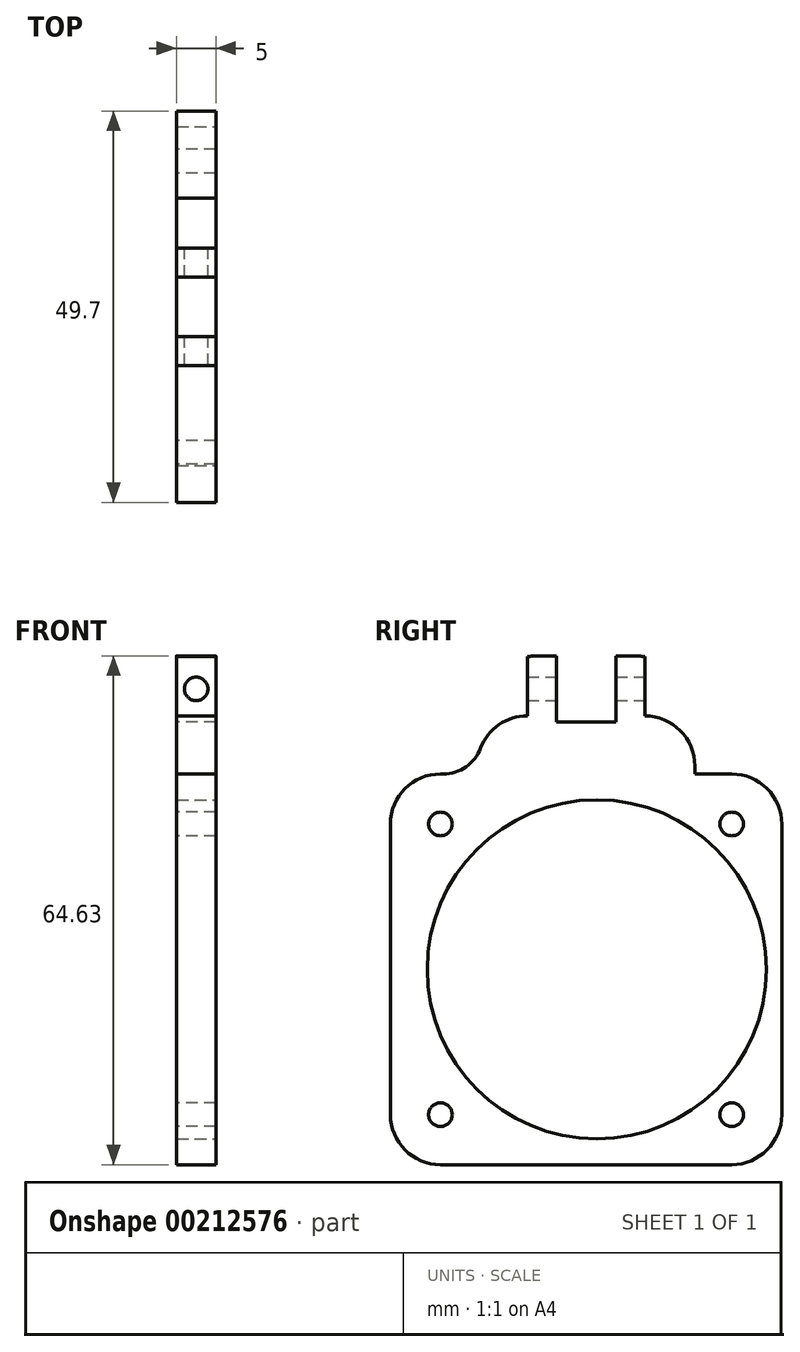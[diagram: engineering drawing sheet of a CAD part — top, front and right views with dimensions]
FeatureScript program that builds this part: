
annotation { "Feature Type Name" : "Feature", "Feature Type Description" : "" }
export const myFeature = defineFeature(function(context is Context, id is Id, definition is map)
    precondition{}
    {
        {
            var Q0;
            Q0=qCreatedBy(makeId("Right.planeOp"),FACE);
            var sketch = newSketch(context, id + "F0", { "sketchPlane" : qUnion([Q0])});
            skCircle(sketch, "E0", {"center": v(0, 0) * mm, "radius": 1.5 * mm});
            skCircle(sketch, "E1", {"center": v(0, -36.93) * mm, "radius": 1.5 * mm});
            skCircle(sketch, "E2", {"center": v(37, -36.93) * mm, "radius": 1.5 * mm});
            skCircle(sketch, "E3", {"center": v(37, 0) * mm, "radius": 1.5 * mm});
            skLineSegment(sketch, "E4", {"start": v(0, 0) * mm, "end": v(0, -36.93) * mm});
            skLineSegment(sketch, "E5.0", {"start": v(-6.35, 0) * mm, "end": v(-6.35, -36.93) * mm});
            skLineSegment(sketch, "E6", {"start": v(0, 0) * mm, "end": v(37, 0) * mm});
            skLineSegment(sketch, "E7", {"start": v(37, -36.93) * mm, "end": v(0, -36.93) * mm});
            skLineSegment(sketch, "E8", {"start": v(37, -36.93) * mm, "end": v(37, -1.5) * mm});
            skLineSegment(sketch, "E9.0", {"start": v(0, 6.35) * mm, "end": v(37, 6.35) * mm});
            skLineSegment(sketch, "E10.0", {"start": v(43.35, -36.93) * mm, "end": v(43.35, 0) * mm});
            skLineSegment(sketch, "E11.0", {"start": v(37, -43.28) * mm, "end": v(0, -43.28) * mm});
            skArc(sketch, "E12.filletArc", {"start": v(-6.35, -36.93) * mm, "mid": v(-4.5, -41.42) * mm, "end": v(0, -43.28) * mm});
            skArc(sketch, "E13.filletArc", {"start": v(37, -43.28) * mm, "mid": v(41.5, -41.42) * mm, "end": v(43.35, -36.93) * mm});
            skArc(sketch, "E14.filletArc", {"start": v(0, 6.35) * mm, "mid": v(-4.5, 4.5) * mm, "end": v(-6.35, 0) * mm});
            skArc(sketch, "E15.filletArc", {"start": v(43.35, 0) * mm, "mid": v(41.5, 4.5) * mm, "end": v(37, 6.35) * mm});
            skSolve(sketch);
        }
        {
            var Q0;
            Q0=qSketchRegion(id+"F0",true);
            var Q1;
            {var subQ5=sQuery(id+"F0.wireOp",EDGE,"E0");var subQ11=sQuery(id+"F0.wireOp",EDGE,"E4");var subQ15=makeQuery(id+"F0.imprint","INTERSECT",VERTEX,{"derivedFrom":[subQ5,subQ11]});Q1=makeQuery(id+"F0.imprint","IMPRINT",FACE,{"disambiguationData":[TD([[makeQuery(id+"F0.imprint","IMPRINT",EDGE,{"disambiguationData":[TD([[subQ15,-1.0]])],"derivedFrom":subQ5}),-1.0]])]});}
            extrude(context, id + "F1", {"entities" : qUnion([Q0, Q1]), "depth" : 5 * mm});
        }
        {
            var Q0;
            Q0=makeQuery(id+"F1.opExtrude","CAP_FACE",FACE,{"disambiguationData":[OSD([sQuery(id+"F0.wireOp",EDGE,"E0"),sQuery(id+"F0.wireOp",EDGE,"E1"),sQuery(id+"F0.wireOp",EDGE,"E2"),sQuery(id+"F0.wireOp",EDGE,"E3"),sQuery(id+"F0.wireOp",EDGE,"E5.0"),sQuery(id+"F0.wireOp",EDGE,"E9.0"),sQuery(id+"F0.wireOp",EDGE,"E10.0"),sQuery(id+"F0.wireOp",EDGE,"E11.0"),sQuery(id+"F0.wireOp",EDGE,"E12.filletArc"),sQuery(id+"F0.wireOp",EDGE,"E13.filletArc"),sQuery(id+"F0.wireOp",EDGE,"E14.filletArc"),sQuery(id+"F0.wireOp",EDGE,"E15.filletArc")])],"isStart":false});
            var sketch = newSketch(context, id + "F2", { "sketchPlane" : qUnion([Q0])});
            skCircle(sketch, "E16", {"center": v(19.86, -18.46) * mm, "radius": 21.54 * mm});
            skPoint(sketch, "E16.centerSnap0", {"position": v(-6.35, -18.46) * mm});
            skSolve(sketch);
        }
        {
            var Q0;
            Q0=makeQuery(id+"F2.imprint","IMPRINT",FACE,{"disambiguationData":[TD([[makeQuery(id+"F2.imprint","IMPRINT",EDGE,{"derivedFrom":sQuery(id+"F2.wireOp",EDGE,"E16")}),1.0]])]});
            extrude(context, id + "F3", {"entities" : qUnion([Q0]), "operationType" : NewBodyOperationType.REMOVE, "endBound" : BoundingType.THROUGH_ALL, "oppositeDirection" : true, "depth" : 25.4 * mm});
        }
        {
            var Q0;
            Q0=makeQuery(id+"F1.opExtrude","SWEPT_FACE",FACE,{"disambiguationData":[OSD([sQuery(id+"F0.wireOp",EDGE,"E9.0")])]});
            var sketch = newSketch(context, id + "F4", { "sketchPlane" : qUnion([Q0])});
            skLineSegment(sketch, "E17.bottom", {"start": v(5, 32.3) * mm, "end": v(0, 32.3) * mm});
            skLineSegment(sketch, "E17.top", {"start": v(5, 4.7) * mm, "end": v(0, 4.7) * mm});
            skLineSegment(sketch, "E17.left", {"start": v(5, 32.3) * mm, "end": v(5, 4.7) * mm});
            skLineSegment(sketch, "E17.right", {"start": v(0, 32.3) * mm, "end": v(0, 4.7) * mm});
            skPoint(sketch, "E17.middle", {"position": v(2.5, 18.5) * mm});
            skPoint(sketch, "E17.middle.positionSnap0", {"position": v(2.5, 37) * mm});
            skPoint(sketch, "E17.middle.positionSnap1", {"position": v(5, 18.5) * mm});
            skPoint(sketch, "E17.centerSnap0", {"position": v(2.5, 37) * mm});
            skPoint(sketch, "E17.centerSnap1", {"position": v(5, 18.5) * mm});
            skSolve(sketch);
        }
        {
            var Q0;
            Q0=qSketchRegion(id+"F4",true);
            extrude(context, id + "F5", {"entities" : qUnion([Q0]), "operationType" : NewBodyOperationType.ADD, "depth" : 15 * mm});
        }
        {
            var Q0;
            Q0=makeQuery(id+"F5.opExtrude","CAP_EDGE",EDGE,{"disambiguationData":[OSD([sQuery(id+"F4.wireOp",EDGE,"E17.bottom")])],"isStart":false});
            var Q1;
            Q1=makeQuery(id+"F5.opExtrude","CAP_EDGE",EDGE,{"disambiguationData":[OSD([sQuery(id+"F4.wireOp",EDGE,"E17.top")])],"isStart":false});
            fillet(context, id + "F6", {"entities" : qUnion([Q0, Q1]), "radius" : 7.62 * mm, "tangentPropagation" : true, "allowEdgeOverflow" : false});
        }
        {
            var Q0;
            Q0=makeQuery(id+"F5.opExtrude","CAP_FACE",FACE,{"disambiguationData":[OSD([sQuery(id+"F4.wireOp",EDGE,"E17.bottom"),sQuery(id+"F4.wireOp",EDGE,"E17.top"),sQuery(id+"F4.wireOp",EDGE,"E17.left"),sQuery(id+"F4.wireOp",EDGE,"E17.right")])],"isStart":false});
            var sketch = newSketch(context, id + "F7", { "sketchPlane" : qUnion([Q0])});
            skLineSegment(sketch, "E18.bottom", {"start": v(5, 22.27) * mm, "end": v(0, 22.27) * mm});
            skLineSegment(sketch, "E18.top", {"start": v(5, 14.73) * mm, "end": v(0, 14.73) * mm});
            skLineSegment(sketch, "E18.left", {"start": v(5, 22.27) * mm, "end": v(5, 14.73) * mm});
            skLineSegment(sketch, "E18.right", {"start": v(0, 22.27) * mm, "end": v(0, 14.73) * mm});
            skPoint(sketch, "E18.middle", {"position": v(2.5, 18.5) * mm});
            skPoint(sketch, "E18.middle.positionSnap0", {"position": v(2.5, 24.69) * mm});
            skPoint(sketch, "E18.middle.positionSnap1", {"position": v(0, 18.5) * mm});
            skPoint(sketch, "E18.centerSnap0", {"position": v(2.5, 24.69) * mm});
            skPoint(sketch, "E18.centerSnap1", {"position": v(0, 18.5) * mm});
            skSolve(sketch);
        }
        {
            var Q0;
            Q0=qSketchRegion(id+"F7",true);
            extrude(context, id + "F8", {"entities" : qUnion([Q0]), "operationType" : NewBodyOperationType.REMOVE, "oppositeDirection" : true, "depth" : 8.38 * mm});
        }
        {
            var Q0;
            Q0=makeQuery(id+"F8.boolean.opBoolean","COPY",FACE,{"derivedFrom":makeQuery(id+"F8.opExtrude","SWEPT_FACE",FACE,{"disambiguationData":[OSD([sQuery(id+"F7.wireOp",EDGE,"E18.top")])]})});
            var sketch = newSketch(context, id + "F9", { "sketchPlane" : qUnion([Q0])});
            skCircle(sketch, "E19", {"center": v(-2.5, 17.16) * mm, "radius": 1.5 * mm});
            skPoint(sketch, "E19.centerSnap0", {"position": v(0, 17.16) * mm});
            skPoint(sketch, "E19.centerSnap1", {"position": v(-2.5, 21.35) * mm});
            skSolve(sketch);
        }
        {
            var Q0;
            Q0=qSketchRegion(id+"F9",true);
            extrude(context, id + "F10", {"entities" : qUnion([Q0]), "operationType" : NewBodyOperationType.REMOVE, "endBound" : BoundingType.THROUGH_ALL, "oppositeDirection" : true, "depth" : 25.4 * mm, "hasSecondDirection" : true, "secondDirectionBound" : SecondDirectionBoundingType.THROUGH_ALL, "secondDirectionOppositeDirection" : false, "secondDirectionDepth" : 25.4 * mm});
        }
        {
            var Q0;
            Q0=makeQuery(id+"F5.opExtrude","SWEPT_FACE",FACE,{"disambiguationData":[OSD([sQuery(id+"F4.wireOp",EDGE,"E17.bottom")])]});
            var sketch = newSketch(context, id + "F11", { "sketchPlane" : qUnion([Q0])});
            skLineSegment(sketch, "E20.bottom", {"start": v(-5, 13.73) * mm, "end": v(2.36, 13.73) * mm});
            skLineSegment(sketch, "E20.top", {"start": v(-5, 25.82) * mm, "end": v(2.36, 25.82) * mm});
            skLineSegment(sketch, "E20.left", {"start": v(-5, 13.73) * mm, "end": v(-5, 25.82) * mm});
            skLineSegment(sketch, "E20.right", {"start": v(2.36, 13.73) * mm, "end": v(2.36, 25.82) * mm});
            skSolve(sketch);
        }
        {
            var Q0;
            Q0=qSketchRegion(id+"F11",true);
            extrude(context, id + "F12", {"entities" : qUnion([Q0]), "operationType" : NewBodyOperationType.REMOVE, "oppositeDirection" : true, "depth" : 6.35 * mm});
        }
        {
            var Q0;
            Q0=makeQuery(id+"F5.opExtrude","SWEPT_FACE",FACE,{"disambiguationData":[OSD([sQuery(id+"F4.wireOp",EDGE,"E17.top")])]});
            var sketch = newSketch(context, id + "F13", { "sketchPlane" : qUnion([Q0])});
            skLineSegment(sketch, "E21.bottom", {"start": v(5, 13.73) * mm, "end": v(-2.13, 13.73) * mm});
            skLineSegment(sketch, "E21.top", {"start": v(5, 34.68) * mm, "end": v(-2.13, 34.68) * mm});
            skLineSegment(sketch, "E21.left", {"start": v(5, 13.73) * mm, "end": v(5, 34.68) * mm});
            skLineSegment(sketch, "E21.right", {"start": v(-2.13, 13.73) * mm, "end": v(-2.13, 34.68) * mm});
            skSolve(sketch);
        }
        {
            var Q0;
            Q0=qSketchRegion(id+"F13",true);
            extrude(context, id + "F14", {"entities" : qUnion([Q0]), "operationType" : NewBodyOperationType.REMOVE, "oppositeDirection" : true, "depth" : 6.35 * mm});
        }
        {
            var Q0;
            {var subQ0=sQuery(id+"F4.wireOp",EDGE,"E17.top");Q0=makeQuery(id+"F14.boolean.opBoolean","MERGE",EDGE,{"derivedFrom":[makeQuery(id+"F6.opFillet","BLEND_EDGE",EDGE,{"blendedFrom":[makeQuery(id+"F5.opExtrude","CAP_EDGE",EDGE,{"disambiguationData":[OSD([subQ0])],"isStart":false}),makeQuery(id+"F5.opExtrude","SWEPT_FACE",FACE,{"disambiguationData":[OSD([subQ0])]})],"blendedInto":[makeQuery(id+"F5.opExtrude","SWEPT_FACE",FACE,{"disambiguationData":[OSD([subQ0])]})]}),makeQuery(id+"F14.opExtrude","CAP_EDGE",EDGE,{"disambiguationData":[OSD([sQuery(id+"F13.wireOp",EDGE,"E21.bottom")])],"isStart":true})]});}
            var Q1;
            {var subQ0=sQuery(id+"F4.wireOp",EDGE,"E17.bottom");Q1=makeQuery(id+"F12.boolean.opBoolean","MERGE",EDGE,{"derivedFrom":[makeQuery(id+"F6.opFillet","BLEND_EDGE",EDGE,{"blendedFrom":[makeQuery(id+"F5.opExtrude","CAP_EDGE",EDGE,{"disambiguationData":[OSD([subQ0])],"isStart":false}),makeQuery(id+"F5.opExtrude","SWEPT_FACE",FACE,{"disambiguationData":[OSD([subQ0])]})],"blendedInto":[makeQuery(id+"F5.opExtrude","SWEPT_FACE",FACE,{"disambiguationData":[OSD([subQ0])]})]}),makeQuery(id+"F12.opExtrude","CAP_EDGE",EDGE,{"disambiguationData":[OSD([sQuery(id+"F11.wireOp",EDGE,"E20.bottom")])],"isStart":true})]});}
            fillet(context, id + "F15", {"entities" : qUnion([Q0, Q1]), "radius" : 6.35 * mm, "tangentPropagation" : true, "allowEdgeOverflow" : false});
        }
        {
            var Q0;
            Q0=makeQuery(id+"F5.opExtrude","CAP_EDGE",EDGE,{"disambiguationData":[OSD([sQuery(id+"F4.wireOp",EDGE,"E17.top")])],"isStart":true});
            var Q1;
            Q1=makeQuery(id+"F5.opExtrude","CAP_EDGE",EDGE,{"disambiguationData":[OSD([sQuery(id+"F4.wireOp",EDGE,"E17.bottom")])],"isStart":true});
            fillet(context, id + "F16", {"entities" : qUnion([Q0, Q1]), "radius" : 5.08 * mm, "tangentPropagation" : true, "allowEdgeOverflow" : false});
        }
    });
